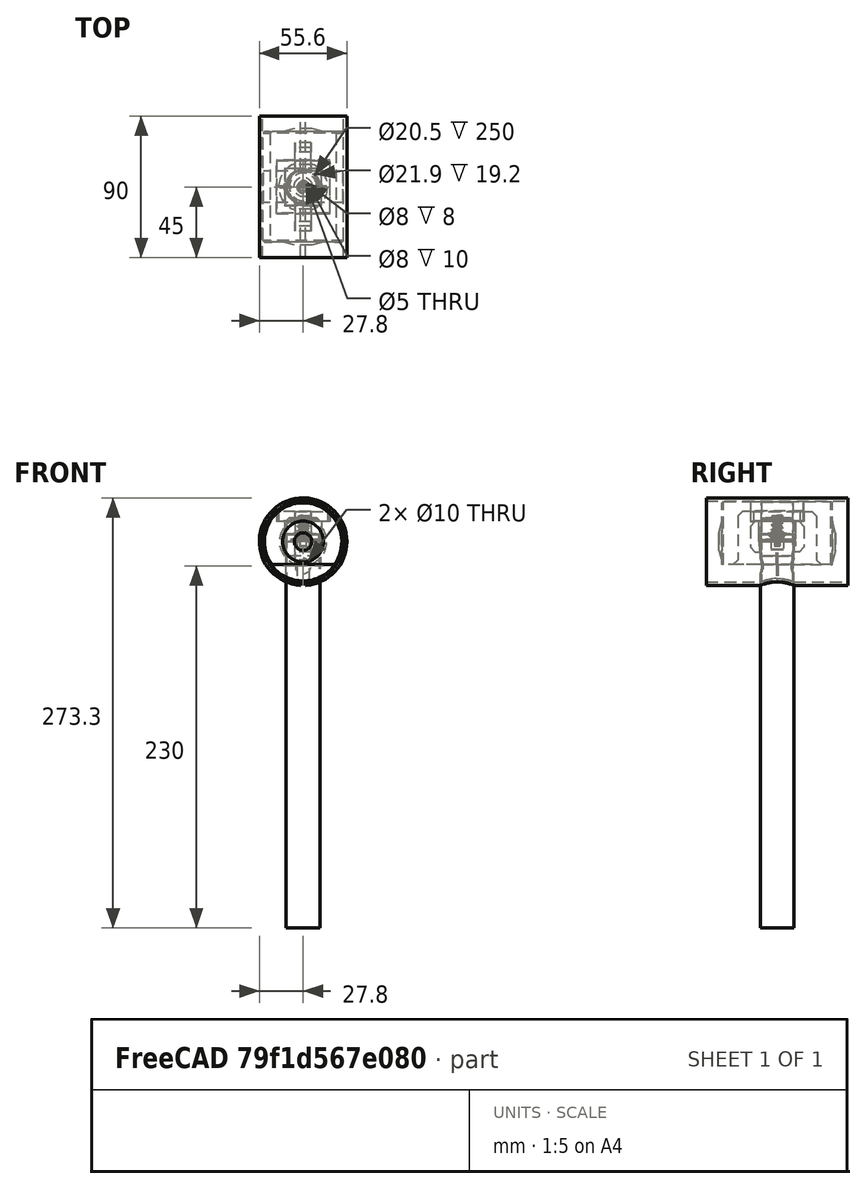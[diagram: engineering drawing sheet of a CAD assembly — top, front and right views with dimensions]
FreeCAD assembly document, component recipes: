
FREECAD ASSEMBLY — COMPONENT RECIPES ("HammerV2")

This assembly document has 14 components, labeled P0..P13 below (a component is one placed body or linked part). 0 of them carry a construction recipe — the FreeCAD feature program that regenerates the part from scratch, quoted from this document or its linked companion documents; the rest are supplied as boundary geometry only. No exploded tour is included for this assembly.
COMPONENT P0 — geometry summary ("FoamL002"; no construction recipe available for this part):
  bounding box: 50.0 x 50.0 x 20.0 mm
  tessellated surface: 500 triangles
  volume: 39270 mm^3 (79% of its bounding box)
  symmetry: 2-fold rotationally symmetric about the x axis; 6-fold rotationally symmetric about the y axis; 2-fold rotationally symmetric about the z axis; mirror-symmetric across its x mid-plane, y mid-plane, z mid-plane
COMPONENT P1 — geometry summary ("FoamL003"; no construction recipe available for this part):
  bounding box: 50.0 x 50.0 x 20.0 mm
  tessellated surface: 500 triangles
  volume: 39270 mm^3 (79% of its bounding box)
  symmetry: 2-fold rotationally symmetric about the x axis; 6-fold rotationally symmetric about the y axis; 2-fold rotationally symmetric about the z axis; mirror-symmetric across its x mid-plane, y mid-plane, z mid-plane
COMPONENT P2 — geometry summary ("FoamS002"; no construction recipe available for this part):
  bounding box: 8.0 x 8.0 x 6.0 mm
  tessellated surface: 500 triangles
  volume: 302 mm^3 (79% of its bounding box)
  symmetry: 2-fold rotationally symmetric about the x axis; 6-fold rotationally symmetric about the z axis; mirror-symmetric across its z mid-plane
COMPONENT P3 — geometry summary ("Handle002"; no construction recipe available for this part):
  bounding box: 250.0 x 21.5 x 21.5 mm
  tessellated surface: 2,028 triangles
  volume: 8142 mm^3 (7% of its bounding box)
  symmetry: 2-fold rotationally symmetric about the x axis; 2-fold rotationally symmetric about the y axis; 2-fold rotationally symmetric about the z axis; mirror-symmetric across its x mid-plane, y mid-plane, z mid-plane
COMPONENT P4 — geometry summary ("Head002"; no construction recipe available for this part):
  bounding box: 74.0 x 51.2 x 40.2 mm
  tessellated surface: 3,312 triangles
  volume: 91439 mm^3 (60% of its bounding box)
  symmetry: 2-fold rotationally symmetric about the z axis; mirror-symmetric across its x mid-plane, y mid-plane
COMPONENT P5 — geometry summary ("HeadTop001"; no construction recipe available for this part):
  bounding box: 33.6 x 33.6 x 12.6 mm
  tessellated surface: 548 triangles
  volume: 7273 mm^3 (51% of its bounding box)
  symmetry: 2-fold rotationally symmetric about the z axis; mirror-symmetric across its x mid-plane, y mid-plane
COMPONENT P6 — geometry summary ("Plug002"; no construction recipe available for this part):
  bounding box: 22.2 x 22.2 x 15.0 mm
  tessellated surface: 3,486 triangles
  volume: 4913 mm^3 (67% of its bounding box)
  symmetry: 6-fold rotationally symmetric about the z axis; mirror-symmetric across its x mid-plane, y mid-plane
COMPONENT P7 — geometry summary ("Sensor002"; no construction recipe available for this part):
  bounding box: 39.5 x 30.0 x 1.0 mm
  tessellated surface: 468 triangles
  volume: 784 mm^3 (66% of its bounding box)
  symmetry: 2-fold rotationally symmetric about the y axis; mirror-symmetric across its x mid-plane, z mid-plane
COMPONENT P8 — geometry summary ("Sensor003"; no construction recipe available for this part):
  bounding box: 39.5 x 30.0 x 1.0 mm
  tessellated surface: 468 triangles
  volume: 784 mm^3 (66% of its bounding box)
  symmetry: 2-fold rotationally symmetric about the y axis; mirror-symmetric across its x mid-plane, z mid-plane
COMPONENT P9 — geometry summary ("Sensor004"; no construction recipe available for this part):
  bounding box: 39.5 x 30.0 x 1.0 mm
  tessellated surface: 468 triangles
  volume: 784 mm^3 (66% of its bounding box)
  symmetry: 2-fold rotationally symmetric about the y axis; mirror-symmetric across its x mid-plane, z mid-plane
COMPONENT P10 — geometry summary ("Shell002"; no construction recipe available for this part):
  bounding box: 90.0 x 55.6 x 55.6 mm
  tessellated surface: 1,570 triangles
  volume: 29157 mm^3 (10% of its bounding box)
  symmetry: 2-fold rotationally symmetric about the z axis; mirror-symmetric across its x mid-plane, y mid-plane
COMPONENT P11 — geometry summary ("Spring002"; no construction recipe available for this part):
  bounding box: 16.2 x 7.0 x 7.0 mm
  tessellated surface: 17,512 triangles
  volume: 94 mm^3 (12% of its bounding box)
COMPONENT P12 — geometry summary ("SpringPusher001"; no construction recipe available for this part):
  bounding box: 23.1 x 23.1 x 14.0 mm
  tessellated surface: 1,594 triangles
  volume: 5227 mm^3 (70% of its bounding box)
  symmetry: 4-fold rotationally symmetric about the z axis; mirror-symmetric across its y mid-plane
COMPONENT P13 — geometry summary ("SpringSeat001"; no construction recipe available for this part):
  bounding box: 8.0 x 8.0 x 4.0 mm
  tessellated surface: 1,222 triangles
  volume: 113 mm^3 (44% of its bounding box)
  symmetry: 6-fold rotationally symmetric about the z axis; mirror-symmetric across its y mid-plane
PROVENANCE & LICENSES
A FreeCAD (.FCStd) document from a public repository crawl; recipes are the document's own serialized feature recipes (and, for linked parts, companion documents' recipes).
License: as declared in the source repository (recorded in the dataset sidecar).
